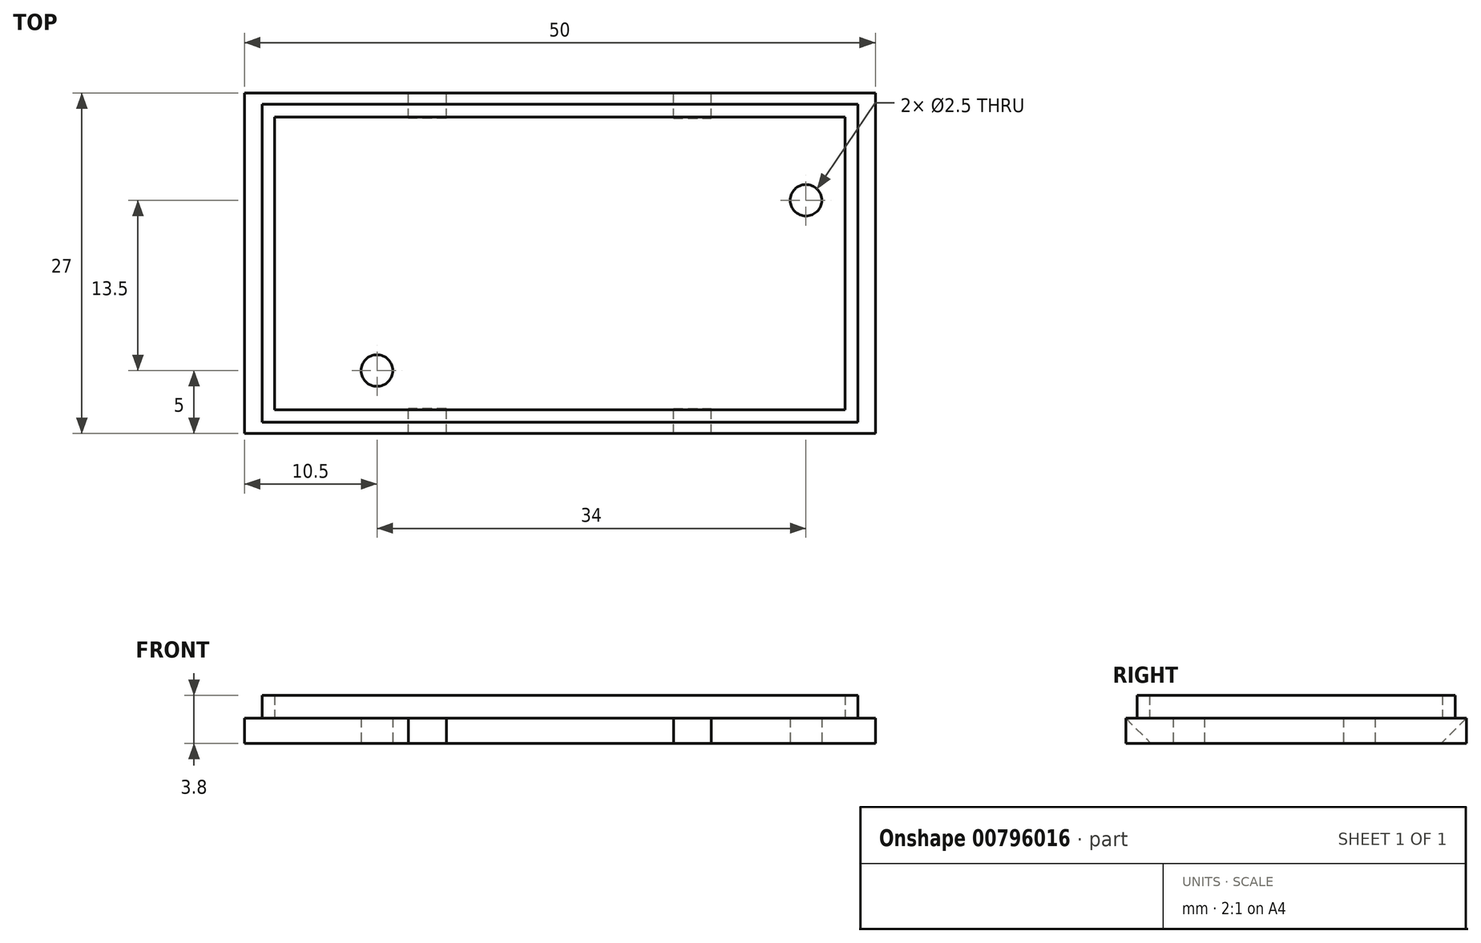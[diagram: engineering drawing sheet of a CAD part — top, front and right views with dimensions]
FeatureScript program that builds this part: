
annotation { "Feature Type Name" : "Feature", "Feature Type Description" : "" }
export const myFeature = defineFeature(function(context is Context, id is Id, definition is map)
    precondition{}
    {
        {
            var Q0;
            Q0=qCreatedBy(makeId("Top.planeOp"),FACE);
            var sketch = newSketch(context, id + "F0", { "sketchPlane" : qUnion([Q0])});
            skLineSegment(sketch, "E0.bottom", {"start": v(25, -13.5) * mm, "end": v(-25, -13.5) * mm});
            skLineSegment(sketch, "E0.top", {"start": v(25, 13.5) * mm, "end": v(-25, 13.5) * mm});
            skLineSegment(sketch, "E0.left", {"start": v(25, -13.5) * mm, "end": v(25, 13.5) * mm});
            skLineSegment(sketch, "E0.right", {"start": v(-25, -13.5) * mm, "end": v(-25, 13.5) * mm});
            skPoint(sketch, "E0.middle", {"position": v(0, 0) * mm});
            skSolve(sketch);
        }
        {
            var Q0;
            Q0 = qSketchRegion(id + "F0", true);
            extrude(context, id + "F1", {"entities" : qUnion([Q0]), "depth" : 2 * mm, "offsetDistance" : 25 * mm});
        }
        {
            var Q0;
            Q0=makeQuery(id+"F1.opExtrude","CAP_FACE",FACE,{"disambiguationData":[OSD([sQuery(id+"F0.wireOp",EDGE,"E0.bottom"),sQuery(id+"F0.wireOp",EDGE,"E0.top"),sQuery(id+"F0.wireOp",EDGE,"E0.left"),sQuery(id+"F0.wireOp",EDGE,"E0.right")])],"isStart":false});
            var sketch = newSketch(context, id + "F2", { "sketchPlane" : qUnion([Q0])});
            skLineSegment(sketch, "E1.bottom", {"start": v(23.6, 11.6) * mm, "end": v(-23.6, 11.6) * mm});
            skLineSegment(sketch, "E1.top", {"start": v(23.6, 12.6) * mm, "end": v(-23.6, 12.6) * mm});
            skLineSegment(sketch, "E1.left", {"start": v(23.6, 11.6) * mm, "end": v(23.6, 12.6) * mm});
            skLineSegment(sketch, "E1.right", {"start": v(-23.6, 11.6) * mm, "end": v(-23.6, 12.6) * mm});
            skPoint(sketch, "E1.middle", {"position": v(0, 12.1) * mm});
            skLineSegment(sketch, "E2.bottom", {"start": v(23.6, -12.6) * mm, "end": v(-23.6, -12.6) * mm});
            skLineSegment(sketch, "E2.top", {"start": v(23.6, -11.6) * mm, "end": v(-23.6, -11.6) * mm});
            skLineSegment(sketch, "E2.left", {"start": v(23.6, -12.6) * mm, "end": v(23.6, -11.6) * mm});
            skLineSegment(sketch, "E2.right", {"start": v(-23.6, -12.6) * mm, "end": v(-23.6, -11.6) * mm});
            skPoint(sketch, "E2.middle", {"position": v(0, -12.1) * mm});
            skLineSegment(sketch, "E3.bottom", {"start": v(-22.6, -11.9) * mm, "end": v(-23.6, -11.9) * mm});
            skLineSegment(sketch, "E3.top", {"start": v(-22.6, 11.9) * mm, "end": v(-23.6, 11.9) * mm});
            skLineSegment(sketch, "E3.left", {"start": v(-22.6, -11.9) * mm, "end": v(-22.6, 11.9) * mm});
            skLineSegment(sketch, "E3.right", {"start": v(-23.6, -11.9) * mm, "end": v(-23.6, 11.9) * mm});
            skPoint(sketch, "E3.middle", {"position": v(-23.1, 0) * mm});
            skLineSegment(sketch, "E4.bottom", {"start": v(23.6, -11.9) * mm, "end": v(22.6, -11.9) * mm});
            skLineSegment(sketch, "E4.top", {"start": v(23.6, 11.9) * mm, "end": v(22.6, 11.9) * mm});
            skLineSegment(sketch, "E4.left", {"start": v(23.6, -11.9) * mm, "end": v(23.6, 11.9) * mm});
            skLineSegment(sketch, "E4.right", {"start": v(22.6, -11.9) * mm, "end": v(22.6, 11.9) * mm});
            skPoint(sketch, "E4.middle", {"position": v(23.1, 0) * mm});
            skSolve(sketch);
        }
        {
            var Q0;
            Q0 = qSketchRegion(id + "F2", true);
            extrude(context, id + "F3", {"entities" : qUnion([Q0]), "operationType" : NewBodyOperationType.ADD, "depth" : 1.8 * mm, "offsetDistance" : 25 * mm});
        }
        {
            var Q0;
            Q0=makeQuery(id+"F1.opExtrude","CAP_FACE",FACE,{"disambiguationData":[OSD([sQuery(id+"F0.wireOp",EDGE,"E0.bottom"),sQuery(id+"F0.wireOp",EDGE,"E0.top"),sQuery(id+"F0.wireOp",EDGE,"E0.left"),sQuery(id+"F0.wireOp",EDGE,"E0.right")])],"isStart":true});
            var sketch = newSketch(context, id + "F4", { "sketchPlane" : qUnion([Q0])});
            skCircle(sketch, "E5", {"center": v(-14.5, 8.5) * mm, "radius": 1.25 * mm});
            skCircle(sketch, "E6", {"center": v(19.5, -5) * mm, "radius": 1.25 * mm});
            skSolve(sketch);
        }
        {
            var Q0;
            Q0 = qSketchRegion(id + "F4", true);
            extrude(context, id + "F5", {"entities" : qUnion([Q0]), "operationType" : NewBodyOperationType.REMOVE, "oppositeDirection" : true, "depth" : 2 * mm, "offsetDistance" : 25 * mm});
        }
        {
            var Q0;
            Q0=qCreatedBy(makeId("Right.planeOp"),FACE);
            var sketch = newSketch(context, id + "F6", { "sketchPlane" : qUnion([Q0])});
            skLineSegment(sketch, "E7", {"start": v(-13.73, 2.22) * mm, "end": v(0, -11.5) * mm});
            skLineSegment(sketch, "E8.MirrorCS", {"start": v(13.73, 2.22) * mm, "end": v(0, -11.5) * mm});
            skLineSegment(sketch, "E9", {"start": v(-13.73, 2.22) * mm, "end": v(-13.73, -11.82) * mm});
            skLineSegment(sketch, "E10", {"start": v(-13.73, -11.82) * mm, "end": v(0, -11.82) * mm});
            skLineSegment(sketch, "E11.MirrorCS", {"start": v(13.73, 2.22) * mm, "end": v(13.73, -11.82) * mm});
            skLineSegment(sketch, "E12.MirrorCS", {"start": v(13.73, -11.82) * mm, "end": v(0, -11.82) * mm});
            skSolve(sketch);
        }
        {
            var Q0;
            Q0=qCreatedBy(makeId("Right.planeOp"),FACE);
            cPlane(context, id + "F7", {"entities" : qUnion([Q0]), "cplaneType" : CPlaneType.OFFSET, "offset" : 12 * mm, "width" : 150 * mm, "height" : 150 * mm});
        }
        {
            var Q0;
            Q0=qCreatedBy(makeId("Right.planeOp"),FACE);
            cPlane(context, id + "F8", {"entities" : qUnion([Q0]), "cplaneType" : CPlaneType.OFFSET, "offset" : 12 * mm, "oppositeDirection" : true, "width" : 150 * mm, "height" : 150 * mm});
        }
        {
            var Q0;
            Q0=qCreatedBy(id+"F7.planeOp",FACE);
            var sketch = newSketch(context, id + "F9", { "sketchPlane" : qUnion([Q0])});
            skLineSegment(sketch, "E13", {"start": v(-13.73, 2.22) * mm, "end": v(0, -11.5) * mm});
            skLineSegment(sketch, "E14.MirrorCS", {"start": v(13.73, 2.22) * mm, "end": v(0, -11.5) * mm});
            skLineSegment(sketch, "E15", {"start": v(-13.73, 2.22) * mm, "end": v(-13.73, -11.82) * mm});
            skLineSegment(sketch, "E16", {"start": v(-13.73, -11.82) * mm, "end": v(0, -11.82) * mm});
            skLineSegment(sketch, "E17.MirrorCS", {"start": v(13.73, 2.22) * mm, "end": v(13.73, -11.82) * mm});
            skLineSegment(sketch, "E18.MirrorCS", {"start": v(13.73, -11.82) * mm, "end": v(0, -11.82) * mm});
            skSolve(sketch);
        }
        {
            var Q0;
            Q0=qCreatedBy(id+"F8.planeOp",FACE);
            var sketch = newSketch(context, id + "F10", { "sketchPlane" : qUnion([Q0])});
            skLineSegment(sketch, "E19", {"start": v(-13.73, 2.22) * mm, "end": v(0, -11.5) * mm});
            skLineSegment(sketch, "E20.MirrorCS", {"start": v(13.73, 2.22) * mm, "end": v(0, -11.5) * mm});
            skLineSegment(sketch, "E21", {"start": v(-13.73, 2.22) * mm, "end": v(-13.73, -11.82) * mm});
            skLineSegment(sketch, "E22", {"start": v(-13.73, -11.82) * mm, "end": v(0, -11.82) * mm});
            skLineSegment(sketch, "E23.MirrorCS", {"start": v(13.73, 2.22) * mm, "end": v(13.73, -11.82) * mm});
            skLineSegment(sketch, "E24.MirrorCS", {"start": v(13.73, -11.82) * mm, "end": v(0, -11.82) * mm});
            skSolve(sketch);
        }
        {
            var Q0;
            Q0 = qSketchRegion(id + "F9", true);
            extrude(context, id + "F11", {"entities" : qUnion([Q0]), "operationType" : NewBodyOperationType.REMOVE, "oppositeDirection" : true, "depth" : 3 * mm, "offsetDistance" : 25 * mm});
        }
        {
            var Q0;
            Q0 = qSketchRegion(id + "F10", true);
            extrude(context, id + "F12", {"entities" : qUnion([Q0]), "operationType" : NewBodyOperationType.REMOVE, "depth" : 3 * mm, "offsetDistance" : 25 * mm});
        }
    });
